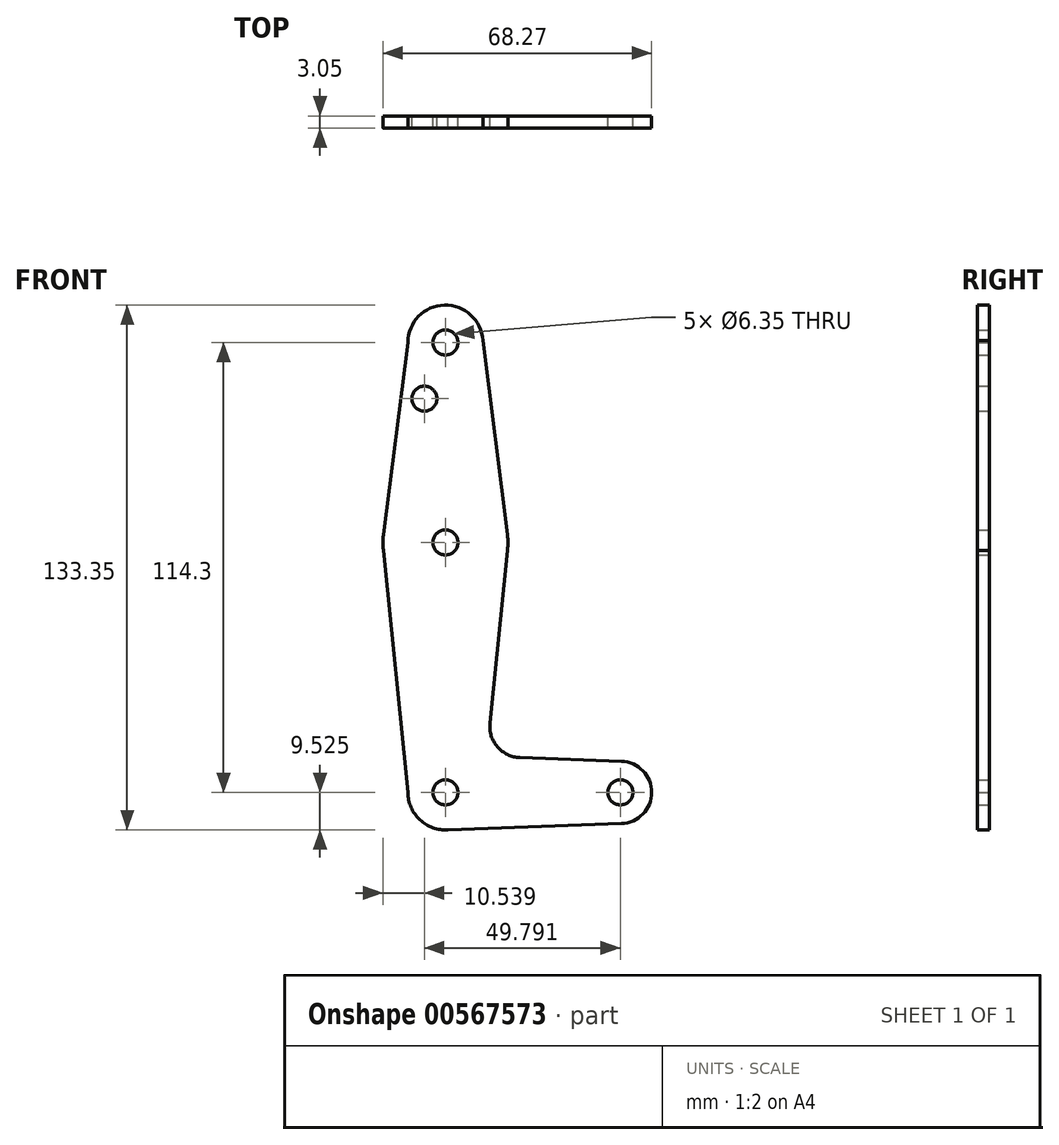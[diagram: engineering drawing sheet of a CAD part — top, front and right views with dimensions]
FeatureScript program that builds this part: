
annotation { "Feature Type Name" : "Feature", "Feature Type Description" : "" }
export const myFeature = defineFeature(function(context is Context, id is Id, definition is map)
    precondition{}
    {
        {
            var Q0;
            Q0=qCreatedBy(makeId("Front.planeOp"),FACE);
            var sketch = newSketch(context, id + "F0", { "sketchPlane" : qUnion([Q0])});
            skCircle(sketch, "E0", {"center": v(0, 6.52) * mm, "radius": 15.88 * mm});
            skCircle(sketch, "E1", {"center": v(0, 57.32) * mm, "radius": 9.53 * mm});
            skCircle(sketch, "E2", {"center": v(0, -56.98) * mm, "radius": 9.53 * mm});
            skCircle(sketch, "E3", {"center": v(44.45, -56.98) * mm, "radius": 7.94 * mm});
            skLineSegment(sketch, "E4", {"start": v(-9.52, 57.38) * mm, "end": v(-15.75, 8.53) * mm});
            skLineSegment(sketch, "E5", {"start": v(-9.53, -56.98) * mm, "end": v(-15.75, 4.52) * mm});
            skLineSegment(sketch, "E6", {"start": v(9.5, 57.9) * mm, "end": v(15.75, 8.52) * mm});
            skLineSegment(sketch, "E7", {"start": v(11.3, -39.38) * mm, "end": v(15.75, 4.53) * mm});
            skLineSegment(sketch, "E8", {"start": v(18.93, -48.12) * mm, "end": v(44.73, -49.04) * mm});
            skLineSegment(sketch, "E9", {"start": v(0, -66.5) * mm, "end": v(44.73, -64.9) * mm});
            skCircle(sketch, "E10", {"center": v(0, 57.32) * mm, "radius": 3.18 * mm});
            skCircle(sketch, "E11", {"center": v(0, 6.52) * mm, "radius": 3.18 * mm});
            skCircle(sketch, "E12", {"center": v(0, -56.98) * mm, "radius": 3.18 * mm});
            skCircle(sketch, "E13", {"center": v(44.45, -56.98) * mm, "radius": 3.18 * mm});
            skLineSegment(sketch, "E14", {"start": v(0, 57.32) * mm, "end": v(0, -56.98) * mm, "construction": true});
            skLineSegment(sketch, "E15", {"start": v(0, -56.98) * mm, "end": v(44.45, -56.98) * mm, "construction": true});
            skCircle(sketch, "E16", {"center": v(-5.34, 43.05) * mm, "radius": 3.18 * mm});
            skArc(sketch, "E17.filletArc", {"start": v(11.3, -39.38) * mm, "mid": v(13.22, -45.4) * mm, "end": v(18.93, -48.12) * mm});
            skCircle(sketch, "E18", {"center": v(0, -56.98) * mm, "radius": 0.84 * mm});
            skSolve(sketch);
        }
        {
            var Q0;
            Q0 = qSketchRegion(id + "F0", true);
            extrude(context, id + "F1", {"entities" : qUnion([Q0]), "depth" : 3.05 * mm, "offsetDistance" : 25.4 * mm});
        }
    });
